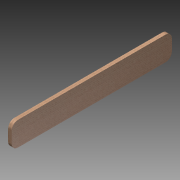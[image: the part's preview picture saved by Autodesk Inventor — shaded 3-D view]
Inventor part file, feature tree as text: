
AUTODESK INVENTOR PART (.ipt)
format: ipt  version: 2014 SP1 (Build 180222100, 222)  size: 99,840 bytes
history: native  units: in
note: dims shown in document units (in); Inventor stores cm internally (conversion verified against a paired STEP export)
features: extrude x1, fillet x1, sketch x1
ambient origin geometry x8: Origin, YZ Plane, XZ Plane, XY Plane, X Axis, Y Axis, Z Axis, Center Point
bodies: Solid1 (feature_tree)
feature tree (3):
  extrude  "Extrusion1"  Depth=0.75in
  fillet  "Fillet1"  Radius=33.375in
  sketch  "Sketch1"  dims[d0=5.0in d1=0.75in d2=33.375in d3=0.0in d4=1.3125in]
